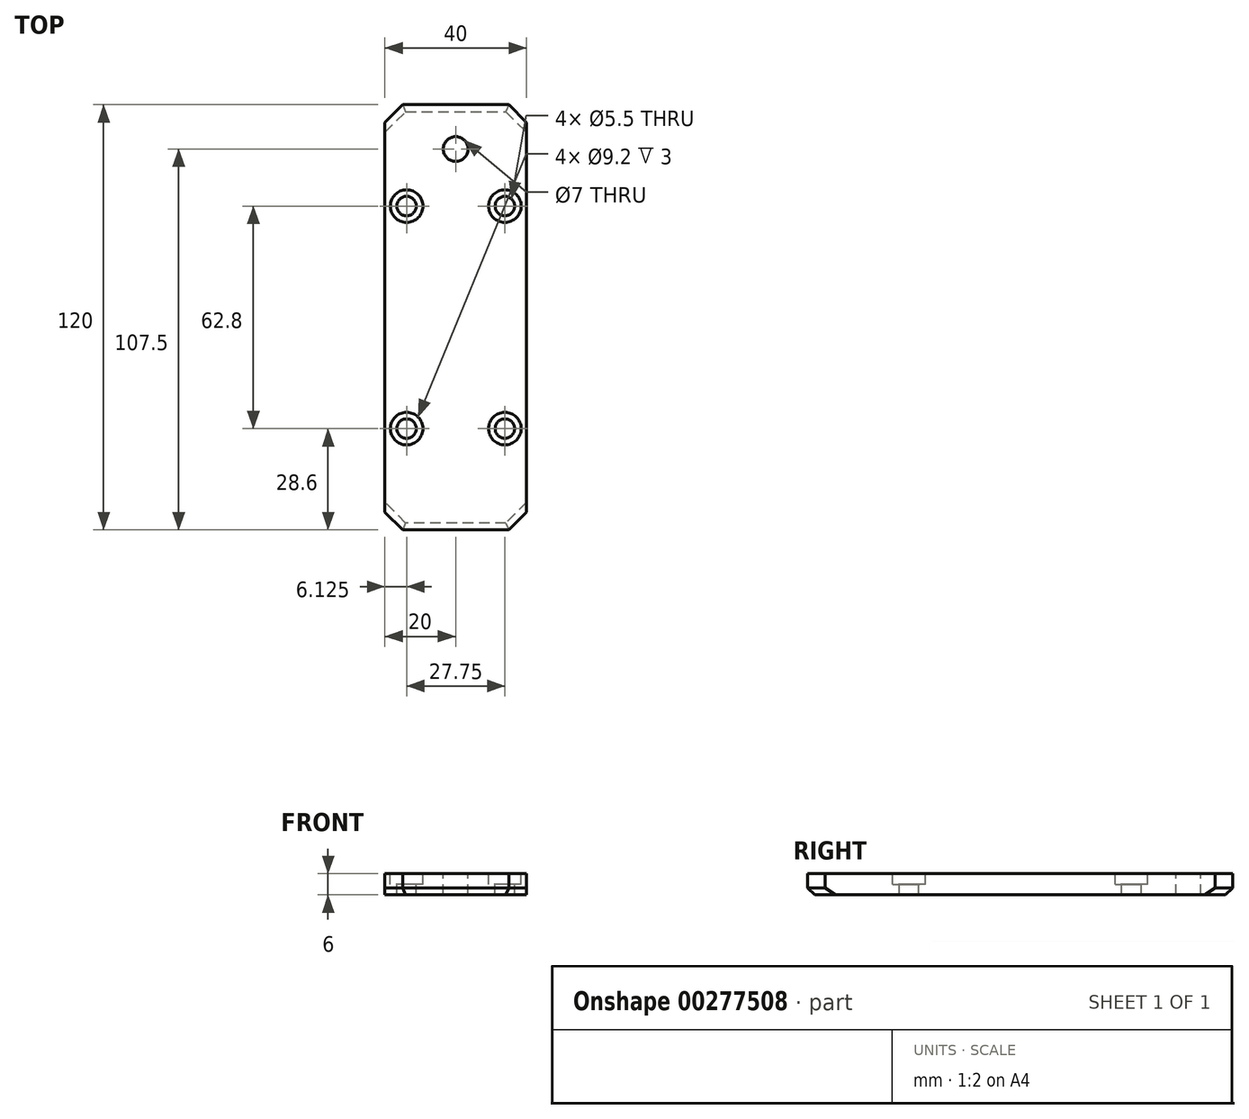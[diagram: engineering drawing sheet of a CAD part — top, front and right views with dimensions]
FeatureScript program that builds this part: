
annotation { "Feature Type Name" : "Feature", "Feature Type Description" : "" }
export const myFeature = defineFeature(function(context is Context, id is Id, definition is map)
    precondition{}
    {
        {
            var Q0;
            Q0=qCreatedBy(makeId("Top.planeOp"),FACE);
            var sketch = newSketch(context, id + "F0", { "sketchPlane" : qUnion([Q0])});
            skLineSegment(sketch, "E0.bottom", {"start": v(20, -60) * mm, "end": v(-20, -60) * mm});
            skLineSegment(sketch, "E0.top", {"start": v(20, 60) * mm, "end": v(-20, 60) * mm});
            skLineSegment(sketch, "E0.left", {"start": v(20, -60) * mm, "end": v(20, 60) * mm});
            skLineSegment(sketch, "E0.right", {"start": v(-20, -60) * mm, "end": v(-20, 60) * mm});
            skPoint(sketch, "E0.middle", {"position": v(0, 0) * mm});
            skSolve(sketch);
        }
        {
            var Q0;
            Q0=makeQuery(id+"F0.imprint","IMPRINT",FACE,{"disambiguationData":[TD([[makeQuery(id+"F0.imprint","IMPRINT",EDGE,{"derivedFrom":sQuery(id+"F0.wireOp",EDGE,"E0.bottom")}),-1.0]])]});
            extrude(context, id + "F1", {"entities" : qUnion([Q0]), "depth" : 6 * mm});
        }
        {
            var Q0;
            Q0=makeQuery(id+"F1.opExtrude","CAP_FACE",FACE,{"disambiguationData":[OSD([sQuery(id+"F0.wireOp",EDGE,"E0.bottom"),sQuery(id+"F0.wireOp",EDGE,"E0.top"),sQuery(id+"F0.wireOp",EDGE,"E0.left"),sQuery(id+"F0.wireOp",EDGE,"E0.right")])],"isStart":false});
            var sketch = newSketch(context, id + "F2", { "sketchPlane" : qUnion([Q0])});
            skLineSegment(sketch, "E1.bottom", {"start": v(13.87, -31.4) * mm, "end": v(-13.88, -31.4) * mm});
            skLineSegment(sketch, "E1.top", {"start": v(13.88, 31.4) * mm, "end": v(-13.87, 31.4) * mm});
            skLineSegment(sketch, "E1.left", {"start": v(13.87, -31.4) * mm, "end": v(13.88, 31.4) * mm});
            skLineSegment(sketch, "E1.right", {"start": v(-13.88, -31.4) * mm, "end": v(-13.87, 31.4) * mm});
            skPoint(sketch, "E1.middle", {"position": v(0, 0) * mm});
            skSolve(sketch);
        }
        {
            var Q0;
            Q0=sQuery(id+"F2.wireOp",VERTEX,"E1.top.end");
            var Q1;
            Q1=sQuery(id+"F2.wireOp",VERTEX,"E1.left.end");
            var Q2;
            Q2=sQuery(id+"F2.wireOp",VERTEX,"E1.right.start");
            var Q3;
            Q3=sQuery(id+"F2.wireOp",VERTEX,"E1.left.start");
            var Q4;
            Q4=makeQuery(id+"F1.opExtrude","SWEPT_BODY",BODY,{"disambiguationData":[OSD([sQuery(id+"F0.wireOp",EDGE,"E0.bottom"),sQuery(id+"F0.wireOp",EDGE,"E0.top"),sQuery(id+"F0.wireOp",EDGE,"E0.left"),sQuery(id+"F0.wireOp",EDGE,"E0.right")])]});
            hole(context, id + "F3", {"style" : HoleStyle.C_BORE, "endStyle" : HoleEndStyle.BLIND, "holeDiameter" : 5.5 * mm, "cBoreDiameter" : 9.2 * mm, "cBoreDepth" : 3 * mm, "holeDepth" : 15 * mm, "tappedDepth" : 12 * mm, "tapClearance" : 3, "locations" : qUnion([Q0, Q1, Q2, Q3]), "scope" : qUnion([Q4])});
        }
        {
            var Q0;
            Q0=makeQuery(id+"F1.opExtrude","CAP_FACE",FACE,{"disambiguationData":[OSD([sQuery(id+"F0.wireOp",EDGE,"E0.bottom"),sQuery(id+"F0.wireOp",EDGE,"E0.top"),sQuery(id+"F0.wireOp",EDGE,"E0.left"),sQuery(id+"F0.wireOp",EDGE,"E0.right")])],"isStart":false});
            var sketch = newSketch(context, id + "F4", { "sketchPlane" : qUnion([Q0])});
            skPoint(sketch, "E2", {"position": v(0, 47.5) * mm});
            skPoint(sketch, "E2.positionSnap0", {"position": v(0, 60) * mm});
            skSolve(sketch);
        }
        {
            var Q0;
            Q0=sQuery(id+"F4.wireOp",VERTEX,"E2");
            var Q1;
            Q1=makeQuery(id+"F1.opExtrude","SWEPT_BODY",BODY,{"disambiguationData":[OSD([sQuery(id+"F0.wireOp",EDGE,"E0.bottom"),sQuery(id+"F0.wireOp",EDGE,"E0.top"),sQuery(id+"F0.wireOp",EDGE,"E0.left"),sQuery(id+"F0.wireOp",EDGE,"E0.right")])]});
            hole(context, id + "F5", {"style" : HoleStyle.SIMPLE, "endStyle" : HoleEndStyle.BLIND, "holeDiameter" : 7 * mm, "holeDepth" : 15 * mm, "tappedDepth" : 12 * mm, "tapClearance" : 3, "locations" : qUnion([Q0]), "scope" : qUnion([Q1])});
        }
        {
            var Q0;
            Q0=makeQuery(id+"F1.opExtrude","SWEPT_EDGE",EDGE,{"disambiguationData":[OSD([sQuery(id+"F0.wireOp",EDGE,"E0.top"),sQuery(id+"F0.wireOp",EDGE,"E0.left")])]});
            var Q1;
            Q1=makeQuery(id+"F1.opExtrude","SWEPT_EDGE",EDGE,{"disambiguationData":[OSD([sQuery(id+"F0.wireOp",EDGE,"E0.top"),sQuery(id+"F0.wireOp",EDGE,"E0.right")])]});
            var Q2;
            Q2=makeQuery(id+"F1.opExtrude","SWEPT_EDGE",EDGE,{"disambiguationData":[OSD([sQuery(id+"F0.wireOp",EDGE,"E0.bottom"),sQuery(id+"F0.wireOp",EDGE,"E0.right")])]});
            var Q3;
            Q3=makeQuery(id+"F1.opExtrude","SWEPT_EDGE",EDGE,{"disambiguationData":[OSD([sQuery(id+"F0.wireOp",EDGE,"E0.bottom"),sQuery(id+"F0.wireOp",EDGE,"E0.left")])]});
            chamfer(context, id + "F6", {"entities" : qUnion([Q0, Q1, Q2, Q3]), "width" : 5 * mm, "tangentPropagation" : true});
        }
        {
            var Q0;
            Q0=makeQuery(id+"F1.opExtrude","CAP_EDGE",EDGE,{"disambiguationData":[OSD([sQuery(id+"F0.wireOp",EDGE,"E0.top")])],"isStart":true});
            var Q1;
            {var subQ0=sQuery(id+"F0.wireOp",EDGE,"E0.right");var subQ1=sQuery(id+"F0.wireOp",EDGE,"E0.top");Q1=makeQuery(id+"F6.opChamfer","BLEND_EDGE",EDGE,{"blendedFrom":[makeQuery(id+"F1.opExtrude","SWEPT_EDGE",EDGE,{"disambiguationData":[OSD([subQ1,subQ0])]}),makeQuery(id+"F1.opExtrude","CAP_FACE",FACE,{"disambiguationData":[OSD([sQuery(id+"F0.wireOp",EDGE,"E0.bottom"),subQ1,sQuery(id+"F0.wireOp",EDGE,"E0.left"),subQ0])],"isStart":true})],"blendedInto":[makeQuery(id+"F1.opExtrude","CAP_FACE",FACE,{"disambiguationData":[OSD([sQuery(id+"F0.wireOp",EDGE,"E0.bottom"),subQ1,sQuery(id+"F0.wireOp",EDGE,"E0.left"),subQ0])],"isStart":true})]});}
            var Q2;
            {var subQ0=sQuery(id+"F0.wireOp",EDGE,"E0.left");var subQ1=sQuery(id+"F0.wireOp",EDGE,"E0.top");Q2=makeQuery(id+"F6.opChamfer","BLEND_EDGE",EDGE,{"blendedFrom":[makeQuery(id+"F1.opExtrude","SWEPT_EDGE",EDGE,{"disambiguationData":[OSD([subQ1,subQ0])]}),makeQuery(id+"F1.opExtrude","CAP_FACE",FACE,{"disambiguationData":[OSD([sQuery(id+"F0.wireOp",EDGE,"E0.bottom"),subQ1,subQ0,sQuery(id+"F0.wireOp",EDGE,"E0.right")])],"isStart":true})],"blendedInto":[makeQuery(id+"F1.opExtrude","CAP_FACE",FACE,{"disambiguationData":[OSD([sQuery(id+"F0.wireOp",EDGE,"E0.bottom"),subQ1,subQ0,sQuery(id+"F0.wireOp",EDGE,"E0.right")])],"isStart":true})]});}
            var Q3;
            {var subQ0=sQuery(id+"F0.wireOp",EDGE,"E0.left");var subQ1=sQuery(id+"F0.wireOp",EDGE,"E0.bottom");Q3=makeQuery(id+"F6.opChamfer","BLEND_EDGE",EDGE,{"blendedFrom":[makeQuery(id+"F1.opExtrude","SWEPT_EDGE",EDGE,{"disambiguationData":[OSD([subQ1,subQ0])]}),makeQuery(id+"F1.opExtrude","CAP_FACE",FACE,{"disambiguationData":[OSD([subQ1,sQuery(id+"F0.wireOp",EDGE,"E0.top"),subQ0,sQuery(id+"F0.wireOp",EDGE,"E0.right")])],"isStart":true})],"blendedInto":[makeQuery(id+"F1.opExtrude","CAP_FACE",FACE,{"disambiguationData":[OSD([subQ1,sQuery(id+"F0.wireOp",EDGE,"E0.top"),subQ0,sQuery(id+"F0.wireOp",EDGE,"E0.right")])],"isStart":true})]});}
            var Q4;
            Q4=makeQuery(id+"F1.opExtrude","CAP_EDGE",EDGE,{"disambiguationData":[OSD([sQuery(id+"F0.wireOp",EDGE,"E0.bottom")])],"isStart":true});
            var Q5;
            {var subQ0=sQuery(id+"F0.wireOp",EDGE,"E0.right");var subQ1=sQuery(id+"F0.wireOp",EDGE,"E0.bottom");Q5=makeQuery(id+"F6.opChamfer","BLEND_EDGE",EDGE,{"blendedFrom":[makeQuery(id+"F1.opExtrude","SWEPT_EDGE",EDGE,{"disambiguationData":[OSD([subQ1,subQ0])]}),makeQuery(id+"F1.opExtrude","CAP_FACE",FACE,{"disambiguationData":[OSD([subQ1,sQuery(id+"F0.wireOp",EDGE,"E0.top"),sQuery(id+"F0.wireOp",EDGE,"E0.left"),subQ0])],"isStart":true})],"blendedInto":[makeQuery(id+"F1.opExtrude","CAP_FACE",FACE,{"disambiguationData":[OSD([subQ1,sQuery(id+"F0.wireOp",EDGE,"E0.top"),sQuery(id+"F0.wireOp",EDGE,"E0.left"),subQ0])],"isStart":true})]});}
            chamfer(context, id + "F7", {"entities" : qUnion([Q0, Q1, Q2, Q3, Q4, Q5]), "width" : 2 * mm, "tangentPropagation" : true});
        }
    });
